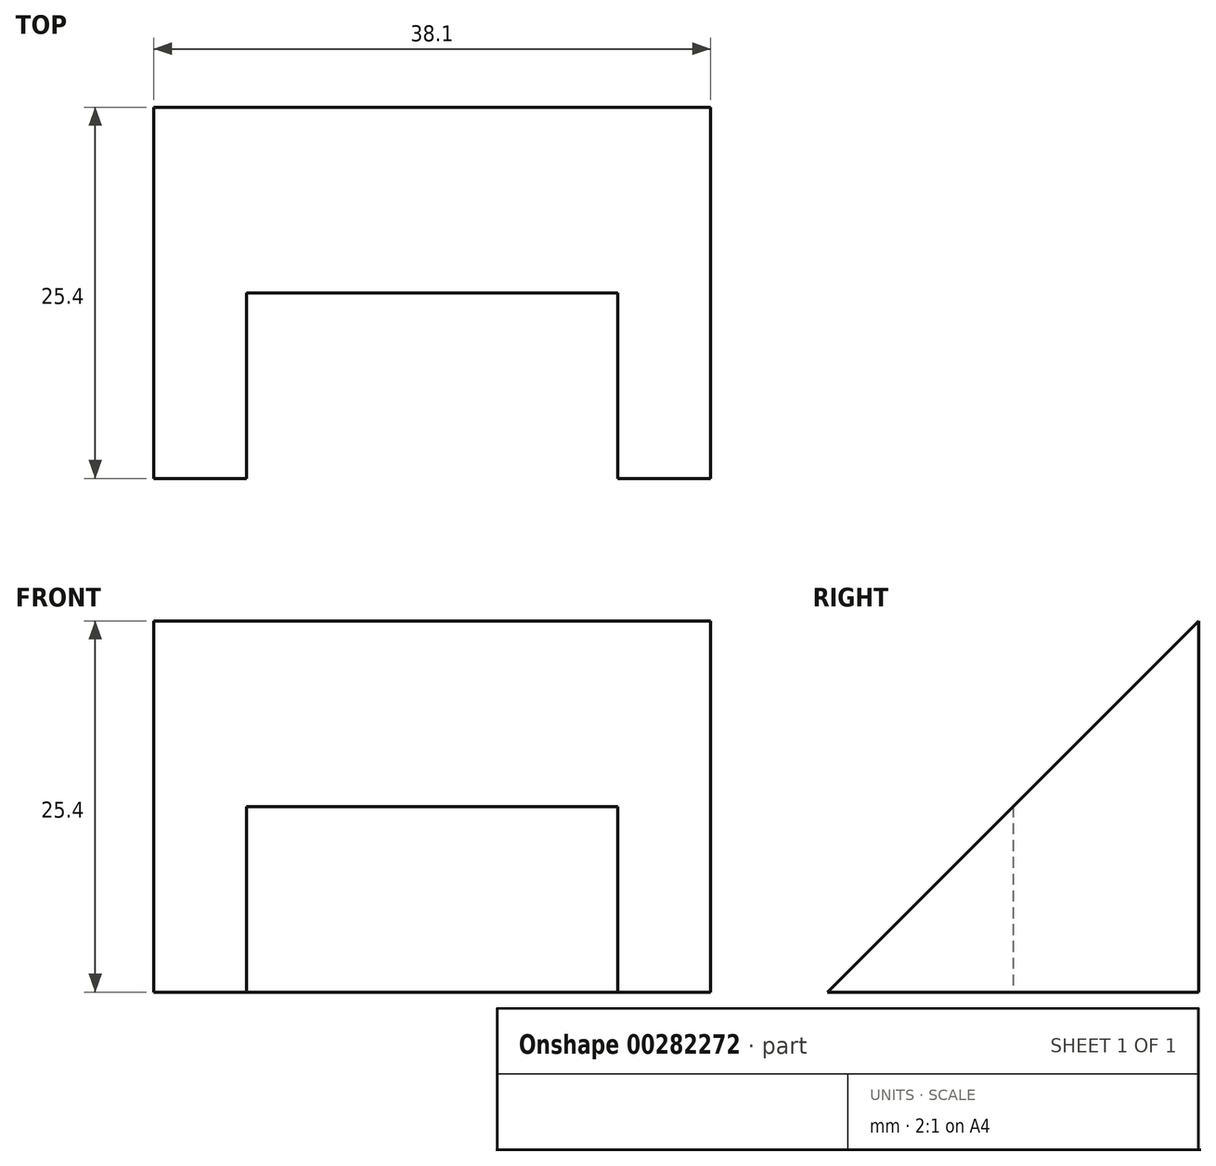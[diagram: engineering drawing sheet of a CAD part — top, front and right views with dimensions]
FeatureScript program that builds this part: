
annotation { "Feature Type Name" : "Feature", "Feature Type Description" : "" }
export const myFeature = defineFeature(function(context is Context, id is Id, definition is map)
    precondition{}
    {
        {
            var Q0;
            Q0=qCreatedBy(makeId("Right.planeOp"),FACE);
            var sketch = newSketch(context, id + "F0", { "sketchPlane" : qUnion([Q0])});
            skLineSegment(sketch, "E0", {"start": v(0, 0) * mm, "end": v(25.4, 0) * mm});
            skLineSegment(sketch, "E1", {"start": v(25.4, 0) * mm, "end": v(25.4, 25.4) * mm});
            skLineSegment(sketch, "E2", {"start": v(25.4, 25.4) * mm, "end": v(0, 0) * mm});
            skSolve(sketch);
        }
        {
            var Q0;
            Q0 = qSketchRegion(id + "F0", true);
            extrude(context, id + "F1", {"entities" : qUnion([Q0]), "oppositeDirection" : true, "depth" : 38.1 * mm});
        }
        {
            var Q0;
            Q0=makeQuery(id+"F1.opExtrude","SWEPT_FACE",FACE,{"disambiguationData":[OSD([sQuery(id+"F0.wireOp",EDGE,"E0")])]});
            var sketch = newSketch(context, id + "F2", { "sketchPlane" : qUnion([Q0])});
            skLineSegment(sketch, "E3.bottom", {"start": v(-31.75, 0) * mm, "end": v(-6.35, 0) * mm});
            skLineSegment(sketch, "E3.top", {"start": v(-31.75, -12.7) * mm, "end": v(-6.35, -12.7) * mm});
            skLineSegment(sketch, "E3.left", {"start": v(-31.75, 0) * mm, "end": v(-31.75, -12.7) * mm});
            skLineSegment(sketch, "E3.right", {"start": v(-6.35, 0) * mm, "end": v(-6.35, -12.7) * mm});
            skSolve(sketch);
        }
        {
            var Q0;
            Q0 = qSketchRegion(id + "F2", true);
            extrude(context, id + "F3", {"entities" : qUnion([Q0]), "operationType" : NewBodyOperationType.REMOVE, "oppositeDirection" : true, "depth" : 12.7 * mm});
        }
    });
